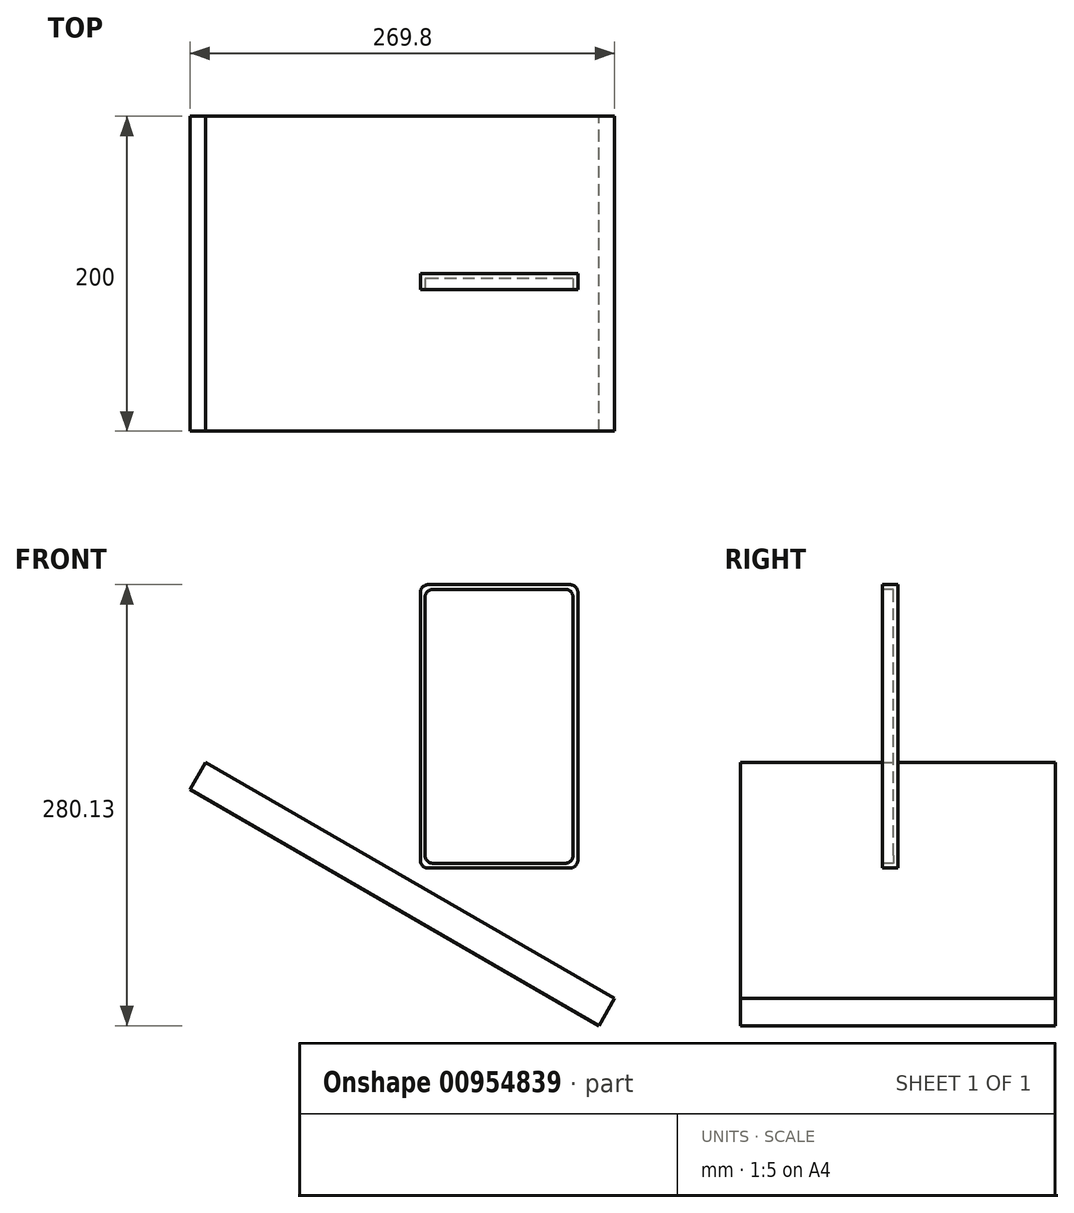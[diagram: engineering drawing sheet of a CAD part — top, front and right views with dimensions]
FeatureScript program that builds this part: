
annotation { "Feature Type Name" : "Feature", "Feature Type Description" : "" }
export const myFeature = defineFeature(function(context is Context, id is Id, definition is map)
    precondition{}
    {
        {
            var Q0;
            Q0=qCreatedBy(makeId("Front.planeOp"),FACE);
            var sketch = newSketch(context, id + "F0", { "sketchPlane" : qUnion([Q0])});
            skLineSegment(sketch, "E0.bottom", {"start": v(50, -90) * mm, "end": v(-50, -90) * mm});
            skLineSegment(sketch, "E0.top", {"start": v(50, 90) * mm, "end": v(-50, 90) * mm});
            skLineSegment(sketch, "E0.left", {"start": v(50, -90) * mm, "end": v(50, 90) * mm});
            skLineSegment(sketch, "E0.right", {"start": v(-50, -90) * mm, "end": v(-50, 90) * mm});
            skPoint(sketch, "E0.middle", {"position": v(0, 0) * mm});
            skSolve(sketch);
        }
        {
            var Q0;
            Q0 = qSketchRegion(id + "F0", true);
            extrude(context, id + "F1", {"entities" : qUnion([Q0]), "depth" : 10 * mm, "offsetDistance" : 25 * mm});
        }
        {
            var Q0;
            Q0=makeQuery(id+"F1.opExtrude","CAP_FACE",FACE,{"disambiguationData":[OSD([sQuery(id+"F0.wireOp",EDGE,"E0.bottom"),sQuery(id+"F0.wireOp",EDGE,"E0.top"),sQuery(id+"F0.wireOp",EDGE,"E0.left"),sQuery(id+"F0.wireOp",EDGE,"E0.right")])],"isStart":false});
            var sketch = newSketch(context, id + "F2", { "sketchPlane" : qUnion([Q0])});
            skLineSegment(sketch, "E1.bottom", {"start": v(47, -87) * mm, "end": v(-47, -87) * mm});
            skLineSegment(sketch, "E1.top", {"start": v(47, 87) * mm, "end": v(-47, 87) * mm});
            skLineSegment(sketch, "E1.left", {"start": v(47, -87) * mm, "end": v(47, 87) * mm});
            skLineSegment(sketch, "E1.right", {"start": v(-47, -87) * mm, "end": v(-47, 87) * mm});
            skPoint(sketch, "E1.middle", {"position": v(0, 0) * mm});
            skSolve(sketch);
        }
        {
            var Q0;
            Q0 = qSketchRegion(id + "F2", true);
            extrude(context, id + "F3", {"entities" : qUnion([Q0]), "operationType" : NewBodyOperationType.REMOVE, "oppositeDirection" : true, "depth" : 7 * mm, "offsetDistance" : 25 * mm});
        }
        {
            var Q0;
            Q0=makeQuery(id+"F1.opExtrude","SWEPT_EDGE",EDGE,{"disambiguationData":[OSD([sQuery(id+"F0.wireOp",EDGE,"E0.bottom"),sQuery(id+"F0.wireOp",EDGE,"E0.right")])]});
            cPlane(context, id + "F4", {"entities" : qUnion([Q0]), "cplaneType" : CPlaneType.LINE_ANGLE, "offset" : 25 * mm, "angle" : 30 * degree, "width" : 150 * mm, "height" : 150 * mm});
        }
        {
            var Q0;
            Q0=qCreatedBy(id+"F4.planeOp",FACE);
            cPlane(context, id + "F5", {"entities" : qUnion([Q0]), "cplaneType" : CPlaneType.OFFSET, "offset" : 30 * mm, "oppositeDirection" : true, "width" : 150 * mm, "height" : 150 * mm});
        }
        {
            var Q0;
            Q0=qCreatedBy(id+"F5.planeOp",FACE);
            var sketch = newSketch(context, id + "F6", { "sketchPlane" : qUnion([Q0])});
            skLineSegment(sketch, "E2.bottom", {"start": v(150, -100) * mm, "end": v(-150, -100) * mm});
            skLineSegment(sketch, "E2.top", {"start": v(150, 100) * mm, "end": v(-150, 100) * mm});
            skLineSegment(sketch, "E2.left", {"start": v(150, -100) * mm, "end": v(150, 100) * mm});
            skLineSegment(sketch, "E2.right", {"start": v(-150, -100) * mm, "end": v(-150, 100) * mm});
            skPoint(sketch, "E2.middle", {"position": v(0, 0) * mm});
            skSolve(sketch);
        }
        {
            var Q0;
            Q0 = qSketchRegion(id + "F6", true);
            extrude(context, id + "F7", {"entities" : qUnion([Q0]), "depth" : 20 * mm, "offsetDistance" : 25 * mm});
        }
        {
            var Q0;
            Q0=makeQuery(id+"F3.boolean.opBoolean","COPY",EDGE,{"derivedFrom":makeQuery(id+"F3.opExtrude","SWEPT_EDGE",EDGE,{"disambiguationData":[OSD([sQuery(id+"F2.wireOp",EDGE,"E1.bottom"),sQuery(id+"F2.wireOp",EDGE,"E1.right")])]})});
            var Q1;
            Q1=makeQuery(id+"F1.opExtrude","SWEPT_EDGE",EDGE,{"disambiguationData":[OSD([sQuery(id+"F0.wireOp",EDGE,"E0.top"),sQuery(id+"F0.wireOp",EDGE,"E0.left")])]});
            var Q2;
            Q2=makeQuery(id+"F1.opExtrude","SWEPT_EDGE",EDGE,{"disambiguationData":[OSD([sQuery(id+"F0.wireOp",EDGE,"E0.top"),sQuery(id+"F0.wireOp",EDGE,"E0.right")])]});
            var Q3;
            Q3=makeQuery(id+"F3.boolean.opBoolean","COPY",EDGE,{"derivedFrom":makeQuery(id+"F3.opExtrude","SWEPT_EDGE",EDGE,{"disambiguationData":[OSD([sQuery(id+"F2.wireOp",EDGE,"E1.top"),sQuery(id+"F2.wireOp",EDGE,"E1.right")])]})});
            var Q4;
            Q4=makeQuery(id+"F3.boolean.opBoolean","COPY",EDGE,{"derivedFrom":makeQuery(id+"F3.opExtrude","SWEPT_EDGE",EDGE,{"disambiguationData":[OSD([sQuery(id+"F2.wireOp",EDGE,"E1.bottom"),sQuery(id+"F2.wireOp",EDGE,"E1.left")])]})});
            var Q5;
            Q5=makeQuery(id+"F1.opExtrude","SWEPT_EDGE",EDGE,{"disambiguationData":[OSD([sQuery(id+"F0.wireOp",EDGE,"E0.bottom"),sQuery(id+"F0.wireOp",EDGE,"E0.right")])]});
            var Q6;
            Q6=makeQuery(id+"F3.boolean.opBoolean","COPY",EDGE,{"derivedFrom":makeQuery(id+"F3.opExtrude","SWEPT_EDGE",EDGE,{"disambiguationData":[OSD([sQuery(id+"F2.wireOp",EDGE,"E1.top"),sQuery(id+"F2.wireOp",EDGE,"E1.left")])]})});
            var Q7;
            Q7=makeQuery(id+"F1.opExtrude","SWEPT_EDGE",EDGE,{"disambiguationData":[OSD([sQuery(id+"F0.wireOp",EDGE,"E0.bottom"),sQuery(id+"F0.wireOp",EDGE,"E0.left")])]});
            fillet(context, id + "F8", {"entities" : qUnion([Q0, Q1, Q2, Q3, Q4, Q5, Q6, Q7]), "radius" : 5 * mm, "tangentPropagation" : true, "allowEdgeOverflow" : false});
        }
    });
